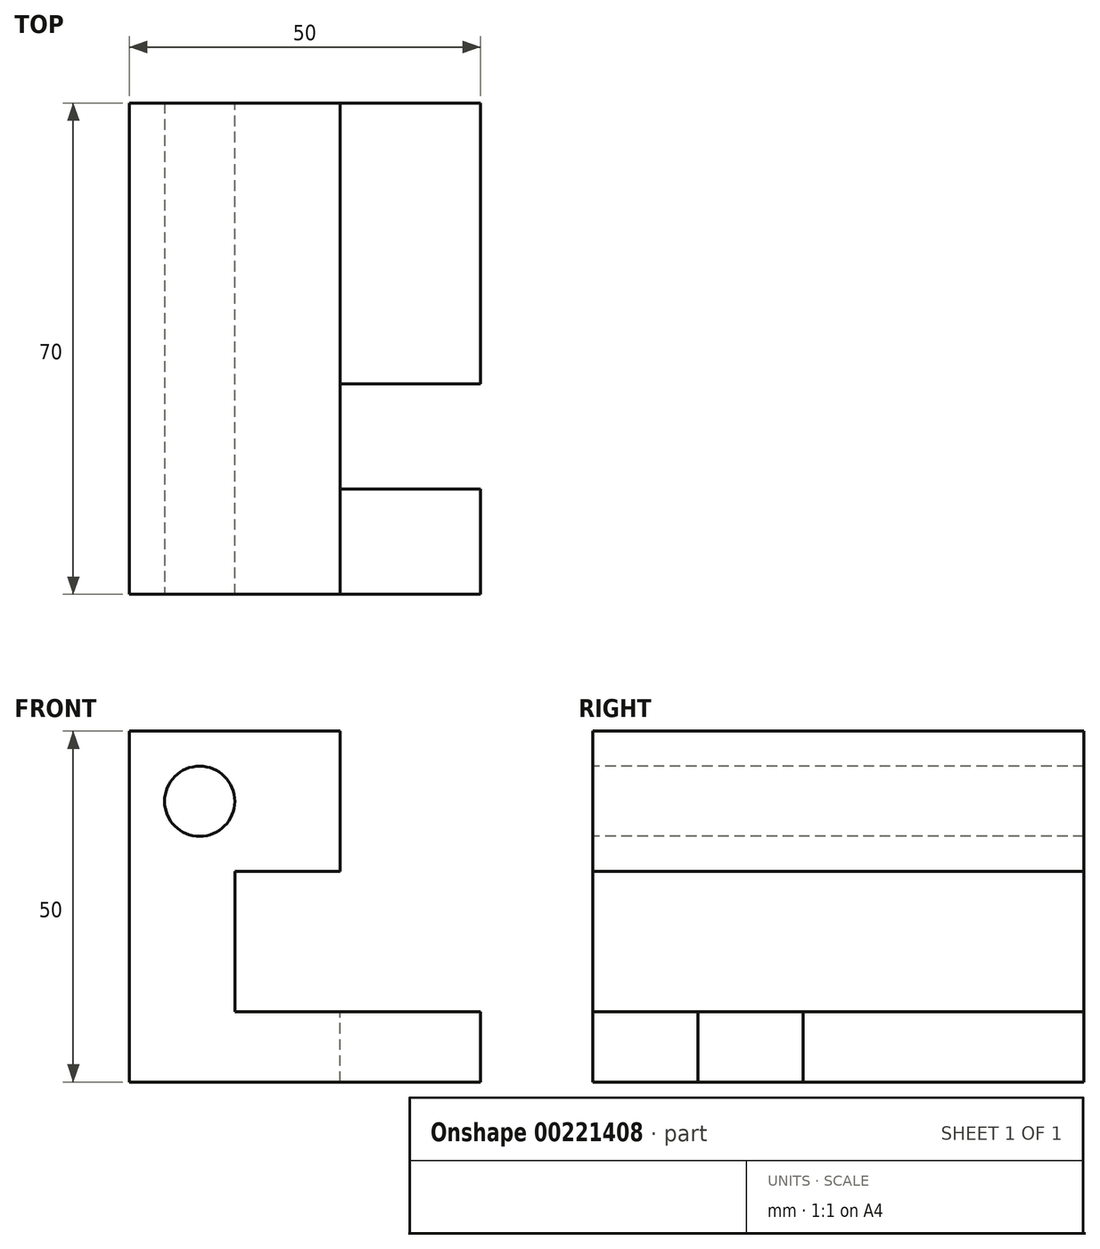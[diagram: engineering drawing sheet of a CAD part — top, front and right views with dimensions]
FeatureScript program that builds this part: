
annotation { "Feature Type Name" : "Feature", "Feature Type Description" : "" }
export const myFeature = defineFeature(function(context is Context, id is Id, definition is map)
    precondition{}
    {
        {
            var Q0;
            Q0=qCreatedBy(makeId("Front.planeOp"),FACE);
            var sketch = newSketch(context, id + "F0", { "sketchPlane" : qUnion([Q0])});
            skLineSegment(sketch, "E0", {"start": v(0, 0) * mm, "end": v(0, 50) * mm});
            skLineSegment(sketch, "E1", {"start": v(0, 50) * mm, "end": v(30, 50) * mm});
            skLineSegment(sketch, "E2", {"start": v(30, 50) * mm, "end": v(30, 30) * mm});
            skLineSegment(sketch, "E3", {"start": v(30, 30) * mm, "end": v(15, 30) * mm});
            skLineSegment(sketch, "E4", {"start": v(15, 30) * mm, "end": v(15, 10) * mm});
            skLineSegment(sketch, "E5", {"start": v(15, 10) * mm, "end": v(50, 10) * mm});
            skLineSegment(sketch, "E6", {"start": v(50, 10) * mm, "end": v(50, 0) * mm});
            skLineSegment(sketch, "E7", {"start": v(50, 0) * mm, "end": v(0, 0) * mm});
            skSolve(sketch);
        }
        {
            var Q0;
            Q0 = qSketchRegion(id + "F0", true);
            extrude(context, id + "F1", {"entities" : qUnion([Q0]), "depth" : 70 * mm});
        }
        {
            var Q0;
            Q0=makeQuery(id+"F1.opExtrude","SWEPT_FACE",FACE,{"disambiguationData":[OSD([sQuery(id+"F0.wireOp",EDGE,"E5")])]});
            var sketch = newSketch(context, id + "F2", { "sketchPlane" : qUnion([Q0])});
            skLineSegment(sketch, "E8.bottom", {"start": v(50, -55) * mm, "end": v(30, -55) * mm});
            skLineSegment(sketch, "E8.top", {"start": v(50, -40) * mm, "end": v(30, -40) * mm});
            skLineSegment(sketch, "E8.left", {"start": v(50, -55) * mm, "end": v(50, -40) * mm});
            skLineSegment(sketch, "E8.right", {"start": v(30, -55) * mm, "end": v(30, -40) * mm});
            skSolve(sketch);
        }
        {
            var Q0;
            Q0 = qSketchRegion(id + "F2", true);
            extrude(context, id + "F3", {"entities" : qUnion([Q0]), "operationType" : NewBodyOperationType.REMOVE, "oppositeDirection" : true, "depth" : 25 * mm});
        }
        {
            var Q0;
            Q0=makeQuery(id+"F1.opExtrude","CAP_FACE",FACE,{"disambiguationData":[OSD([sQuery(id+"F0.wireOp",EDGE,"E0"),sQuery(id+"F0.wireOp",EDGE,"E1"),sQuery(id+"F0.wireOp",EDGE,"E2"),sQuery(id+"F0.wireOp",EDGE,"E3"),sQuery(id+"F0.wireOp",EDGE,"E4"),sQuery(id+"F0.wireOp",EDGE,"E5"),sQuery(id+"F0.wireOp",EDGE,"E6"),sQuery(id+"F0.wireOp",EDGE,"E7")])],"isStart":false});
            var sketch = newSketch(context, id + "F4", { "sketchPlane" : qUnion([Q0])});
            skCircle(sketch, "E9", {"center": v(10, 40) * mm, "radius": 5 * mm});
            skSolve(sketch);
        }
        {
            var Q0;
            Q0 = qSketchRegion(id + "F4", true);
            extrude(context, id + "F5", {"entities" : qUnion([Q0]), "operationType" : NewBodyOperationType.REMOVE, "endBound" : BoundingType.THROUGH_ALL, "oppositeDirection" : true, "depth" : 50 * mm});
        }
    });
